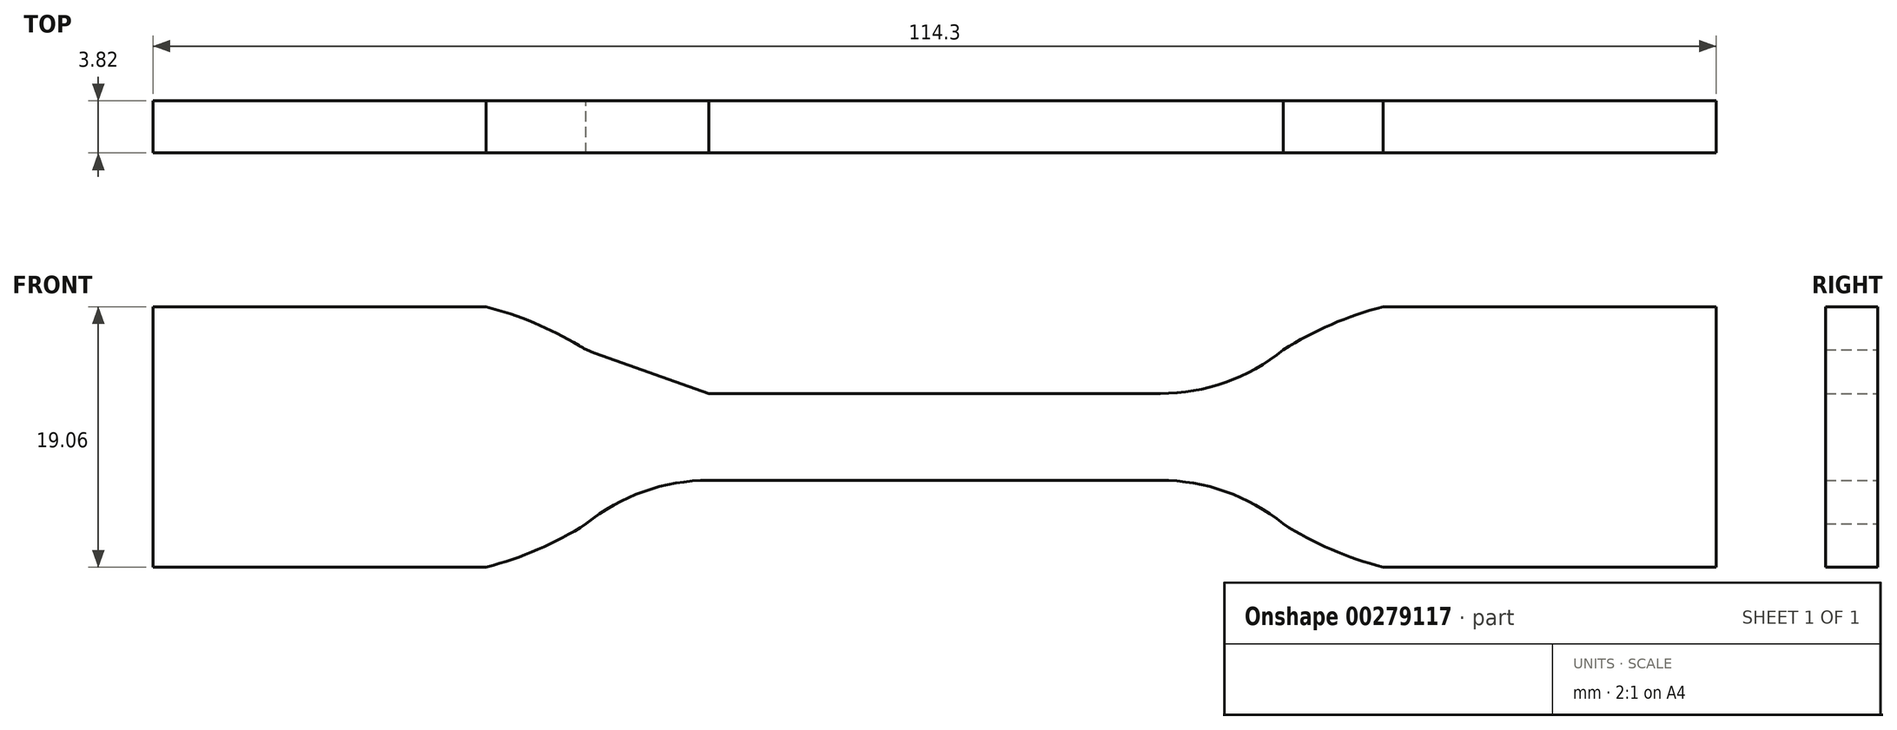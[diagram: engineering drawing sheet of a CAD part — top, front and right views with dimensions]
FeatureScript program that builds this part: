
annotation { "Feature Type Name" : "Feature", "Feature Type Description" : "" }
export const myFeature = defineFeature(function(context is Context, id is Id, definition is map)
    precondition{}
    {
        {
            var Q0;
            Q0=qCreatedBy(makeId("Front.planeOp"),FACE);
            var sketch = newSketch(context, id + "F0", { "sketchPlane" : qUnion([Q0])});
            skLineSegment(sketch, "E0", {"start": v(0, 0) * mm, "end": v(0, 3.18) * mm});
            skLineSegment(sketch, "E1", {"start": v(0, 3.18) * mm, "end": v(16.51, 3.18) * mm});
            skArc(sketch, "E2", {"start": v(16.51, 3.17) * mm, "mid": v(21.27, 4) * mm, "end": v(25.48, 6.36) * mm});
            skArc(sketch, "E3", {"start": v(32.79, 9.52) * mm, "mid": v(29.01, 8.23) * mm, "end": v(25.48, 6.36) * mm});
            skLineSegment(sketch, "E4", {"start": v(32.79, 9.52) * mm, "end": v(57.15, 9.53) * mm});
            skLineSegment(sketch, "E5", {"start": v(57.15, 0) * mm, "end": v(57.15, 9.52) * mm});
            skArc(sketch, "E6.MirrorCS", {"start": v(16.51, -3.17) * mm, "mid": v(21.27, -4) * mm, "end": v(25.48, -6.36) * mm});
            skArc(sketch, "E7.MirrorCS", {"start": v(32.79, -9.52) * mm, "mid": v(29.01, -8.23) * mm, "end": v(25.48, -6.36) * mm});
            skLineSegment(sketch, "E8.MirrorCS", {"start": v(32.79, -9.53) * mm, "end": v(57.15, -9.52) * mm});
            skLineSegment(sketch, "E9.MirrorCS", {"start": v(0, -3.18) * mm, "end": v(16.51, -3.18) * mm});
            skLineSegment(sketch, "E10.MirrorCS", {"start": v(57.15, 0) * mm, "end": v(57.15, -9.52) * mm});
            skLineSegment(sketch, "E11.MirrorCS", {"start": v(0, 0) * mm, "end": v(0, -3.18) * mm});
            skLineSegment(sketch, "E12.MirrorCS", {"start": v(0, 3.18) * mm, "end": v(-16.51, 3.18) * mm});
            skArc(sketch, "E13.MirrorCS", {"start": v(-32.79, 9.52) * mm, "mid": v(-29.29, 8.35) * mm, "end": v(-26, 6.68) * mm});
            skLineSegment(sketch, "E14.MirrorCS", {"start": v(-32.79, 9.52) * mm, "end": v(-57.15, 9.53) * mm});
            skLineSegment(sketch, "E15.MirrorCS", {"start": v(-32.79, -9.53) * mm, "end": v(-57.15, -9.52) * mm});
            skLineSegment(sketch, "E16.MirrorCS", {"start": v(0, -3.18) * mm, "end": v(-16.51, -3.18) * mm});
            skLineSegment(sketch, "E17.MirrorCS", {"start": v(-57.15, 0) * mm, "end": v(-57.15, 9.52) * mm});
            skLineSegment(sketch, "E18.MirrorCS", {"start": v(-57.15, 0) * mm, "end": v(-57.15, -9.52) * mm});
            skArc(sketch, "E19.MirrorCS", {"start": v(-32.79, -9.52) * mm, "mid": v(-29.01, -8.23) * mm, "end": v(-25.48, -6.36) * mm});
            skArc(sketch, "E20.MirrorCS", {"start": v(-16.51, -3.17) * mm, "mid": v(-21.27, -4) * mm, "end": v(-25.48, -6.36) * mm});
            skLineSegment(sketch, "E21", {"start": v(-16.51, 3.18) * mm, "end": v(-24.85, 6.14) * mm});
            skPoint(sketch, "E22.visualSharp", {"position": v(-25.48, 6.36) * mm});
            skArc(sketch, "E22.filletArc", {"start": v(-26, 6.68) * mm, "mid": v(-25.44, 6.38) * mm, "end": v(-24.85, 6.14) * mm});
            skSolve(sketch);
        }
        {
            var Q0;
            Q0 = qSketchRegion(id + "F0", true);
            extrude(context, id + "F1", {"entities" : qUnion([Q0]), "endBound" : BoundingType.SYMMETRIC, "depth" : 3.8 * mm});
        }
    });
